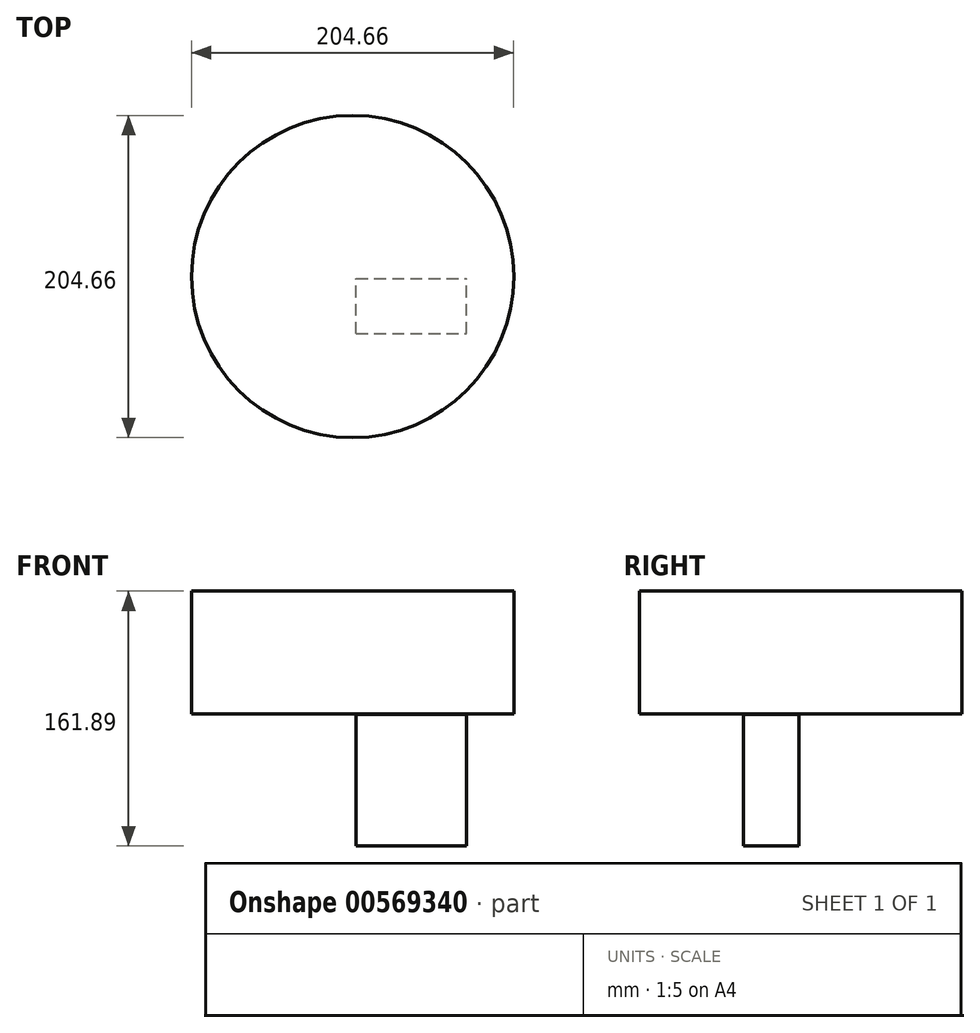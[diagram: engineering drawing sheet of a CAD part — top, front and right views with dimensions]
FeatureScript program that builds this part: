
annotation { "Feature Type Name" : "Feature", "Feature Type Description" : "" }
export const myFeature = defineFeature(function(context is Context, id is Id, definition is map)
    precondition{}
    {
        {
            var Q0;
            Q0=qCreatedBy(makeId("Top.planeOp"),FACE);
            var sketch = newSketch(context, id + "F0", { "sketchPlane" : qUnion([Q0])});
            skCircle(sketch, "E0", {"center": v(-1.97, 1.3) * mm, "radius": 102.33 * mm});
            skSolve(sketch);
        }
        {
            var Q0;
            Q0 = qSketchRegion(id + "F0", true);
            extrude(context, id + "F1", {"entities" : qUnion([Q0]), "depth" : 78 * mm, "offsetDistance" : 25 * mm});
        }
        {
            var Q0;
            Q0=qCreatedBy(makeId("Front.planeOp"),FACE);
            var sketch = newSketch(context, id + "F2", { "sketchPlane" : qUnion([Q0])});
            skLineSegment(sketch, "E1.bottom", {"start": v(0.2, -0.36) * mm, "end": v(70.34, -0.36) * mm});
            skLineSegment(sketch, "E1.top", {"start": v(0.2, -83.89) * mm, "end": v(70.34, -83.89) * mm});
            skLineSegment(sketch, "E1.left", {"start": v(0.2, -0.36) * mm, "end": v(0.2, -83.89) * mm});
            skLineSegment(sketch, "E1.right", {"start": v(70.34, -0.36) * mm, "end": v(70.34, -83.89) * mm});
            skSolve(sketch);
        }
        {
            var Q0;
            Q0 = qSketchRegion(id + "F2", true);
            extrude(context, id + "F3", {"entities" : qUnion([Q0]), "depth" : 35 * mm, "offsetDistance" : 25 * mm});
        }
    });
